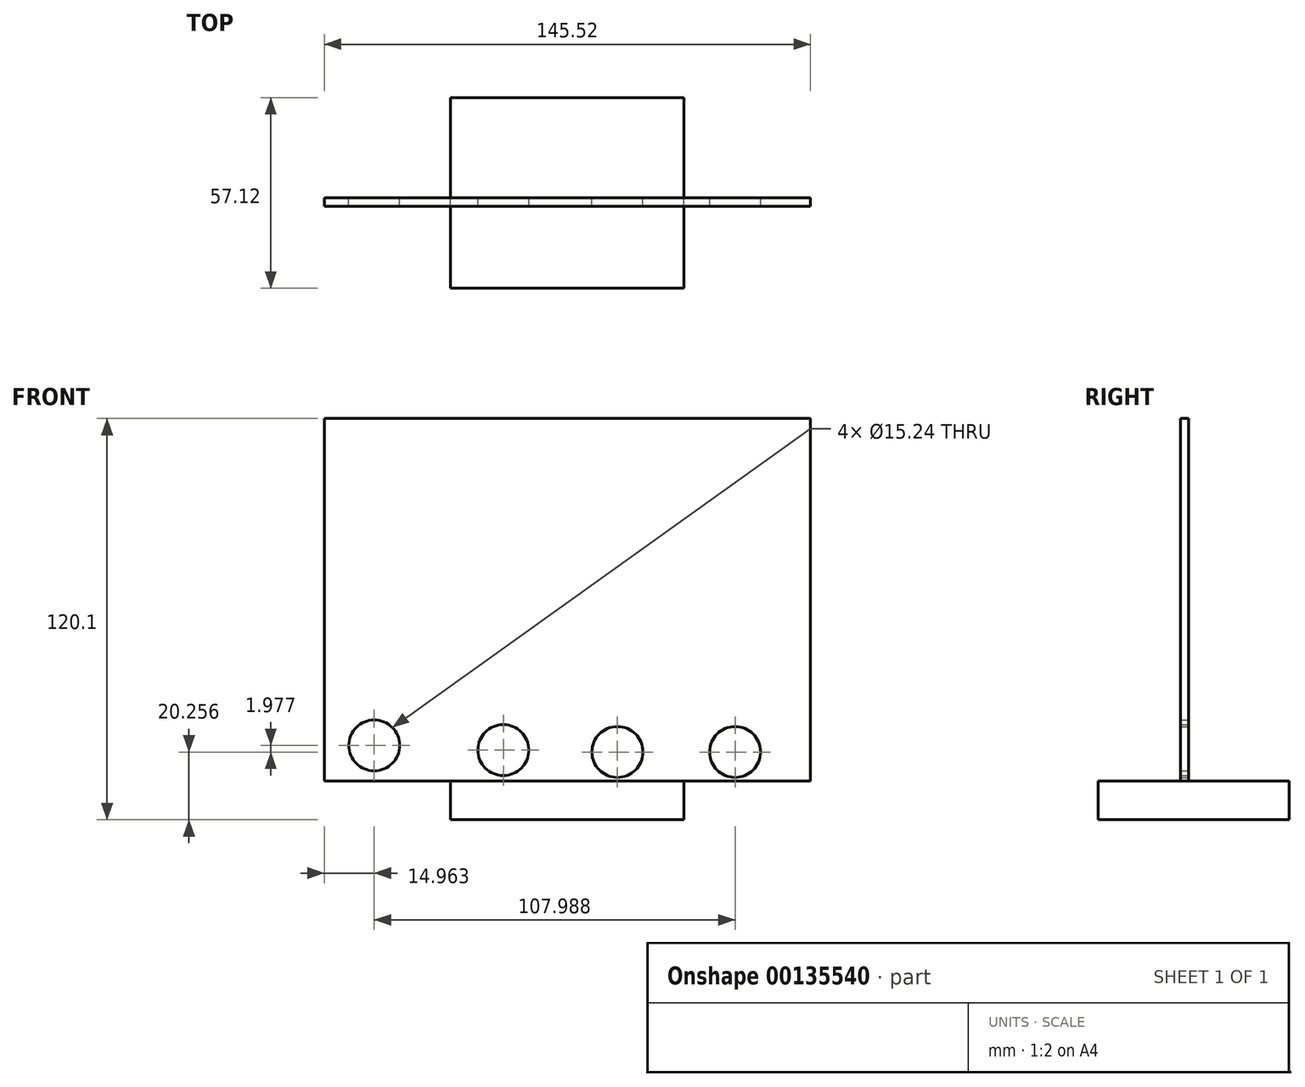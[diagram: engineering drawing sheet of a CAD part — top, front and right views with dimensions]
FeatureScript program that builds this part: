
annotation { "Feature Type Name" : "Feature", "Feature Type Description" : "" }
export const myFeature = defineFeature(function(context is Context, id is Id, definition is map)
    precondition{}
    {
        {
            var Q0;
            Q0=qCreatedBy(makeId("Front.planeOp"),FACE);
            var sketch = newSketch(context, id + "F0", { "sketchPlane" : qUnion([Q0])});
            skLineSegment(sketch, "E0.bottom", {"start": v(-73.33, 54.84) * mm, "end": v(72.2, 54.84) * mm});
            skLineSegment(sketch, "E0.top", {"start": v(-73.33, -53.74) * mm, "end": v(72.2, -53.74) * mm});
            skLineSegment(sketch, "E0.left", {"start": v(-73.33, 54.84) * mm, "end": v(-73.33, -53.74) * mm});
            skLineSegment(sketch, "E0.right", {"start": v(72.2, 54.84) * mm, "end": v(72.2, -53.74) * mm});
            skLineSegment(sketch, "E1", {"start": v(-73.33, -31.46) * mm, "end": v(72.2, -31.46) * mm});
            skCircle(sketch, "E2", {"center": v(-58.37, -43.03) * mm, "radius": 7.62 * mm});
            skCircle(sketch, "E3", {"center": v(-19.73, -44.44) * mm, "radius": 7.62 * mm});
            skCircle(sketch, "E4", {"center": v(14.39, -45) * mm, "radius": 7.62 * mm});
            skCircle(sketch, "E5", {"center": v(49.62, -45) * mm, "radius": 7.62 * mm});
            skSolve(sketch);
        }
        {
            var Q0;
            Q0 = qSketchRegion(id + "F0", true);
            extrude(context, id + "F1", {"entities" : qUnion([Q0]), "depth" : 2.45 * mm});
        }
        {
            var Q0;
            Q0=makeQuery(id+"F1.opExtrude","SWEPT_FACE",FACE,{"disambiguationData":[OSD([sQuery(id+"F0.wireOp",EDGE,"E0.top")])]});
            var sketch = newSketch(context, id + "F2", { "sketchPlane" : qUnion([Q0])});
            skLineSegment(sketch, "E6.bottom", {"start": v(-35.5, 27.04) * mm, "end": v(34.34, 27.04) * mm});
            skLineSegment(sketch, "E6.top", {"start": v(-35.5, -30.08) * mm, "end": v(34.34, -30.08) * mm});
            skLineSegment(sketch, "E6.left", {"start": v(-35.5, 27.04) * mm, "end": v(-35.5, -30.08) * mm});
            skLineSegment(sketch, "E6.right", {"start": v(34.34, 27.04) * mm, "end": v(34.34, -30.08) * mm});
            skSolve(sketch);
        }
        {
            var Q0;
            Q0 = qSketchRegion(id + "F2", true);
            extrude(context, id + "F3", {"entities" : qUnion([Q0]), "operationType" : NewBodyOperationType.ADD, "depth" : 11.52 * mm});
        }
    });
